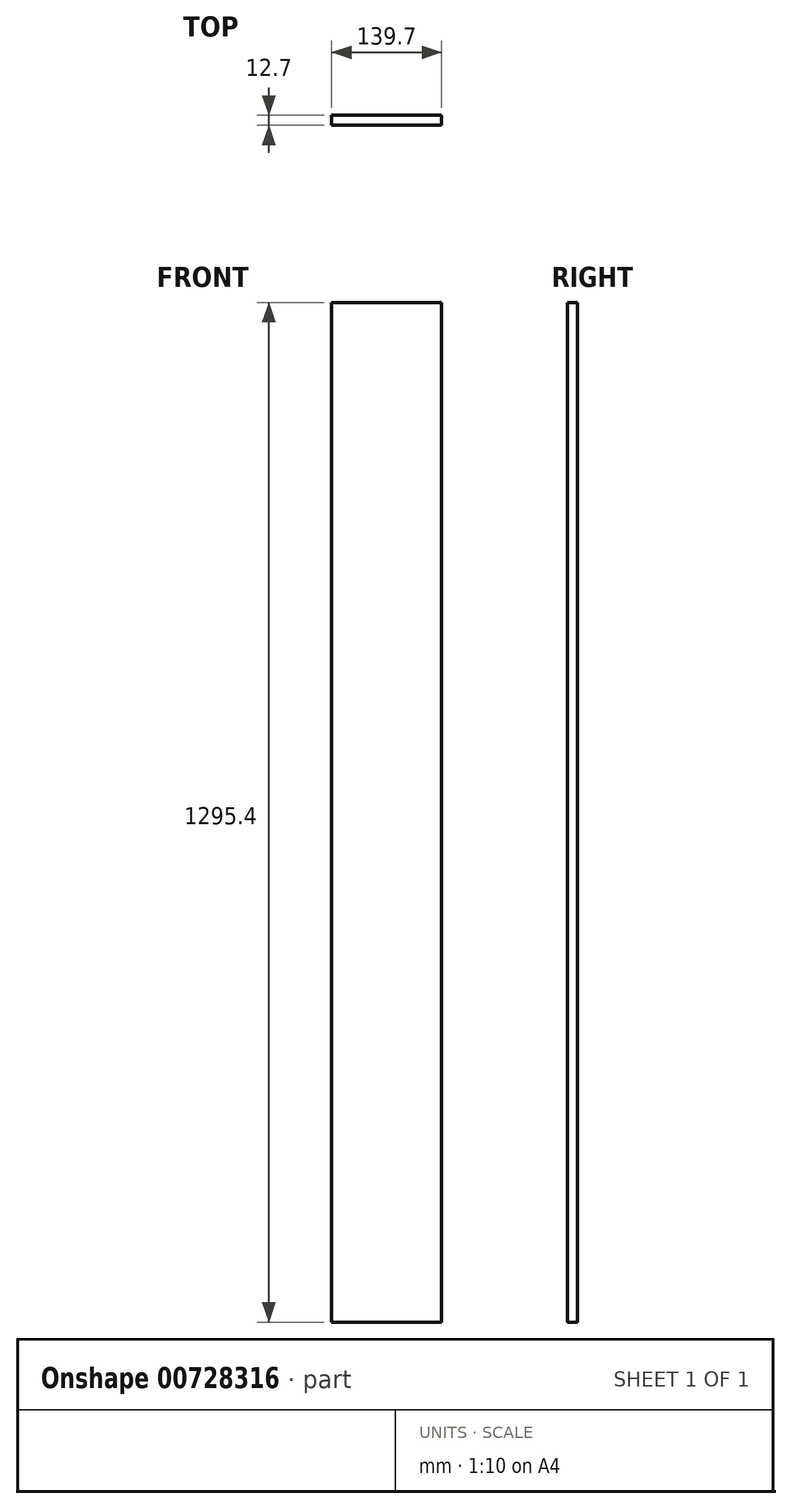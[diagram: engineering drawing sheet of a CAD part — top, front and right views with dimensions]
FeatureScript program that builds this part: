
annotation { "Feature Type Name" : "Feature", "Feature Type Description" : "" }
export const myFeature = defineFeature(function(context is Context, id is Id, definition is map)
    precondition{}
    {
        {
            var Q0;
            Q0=qCreatedBy(makeId("Front.planeOp"),FACE);
            var sketch = newSketch(context, id + "F0", { "sketchPlane" : qUnion([Q0])});
            skLineSegment(sketch, "E0.bottom", {"start": v(69.85, -647.7) * mm, "end": v(-69.85, -647.7) * mm});
            skLineSegment(sketch, "E0.top", {"start": v(69.85, 647.7) * mm, "end": v(-69.85, 647.7) * mm});
            skLineSegment(sketch, "E0.left", {"start": v(69.85, -647.7) * mm, "end": v(69.85, 647.7) * mm});
            skLineSegment(sketch, "E0.right", {"start": v(-69.85, -647.7) * mm, "end": v(-69.85, 647.7) * mm});
            skPoint(sketch, "E0.middle", {"position": v(0, 0) * mm});
            skSolve(sketch);
        }
        {
            var Q0;
            Q0=qSketchRegion(id+"F0",true);
            extrude(context, id + "F1", {"entities" : qUnion([Q0]), "depth" : 12.7 * mm});
        }
    });
